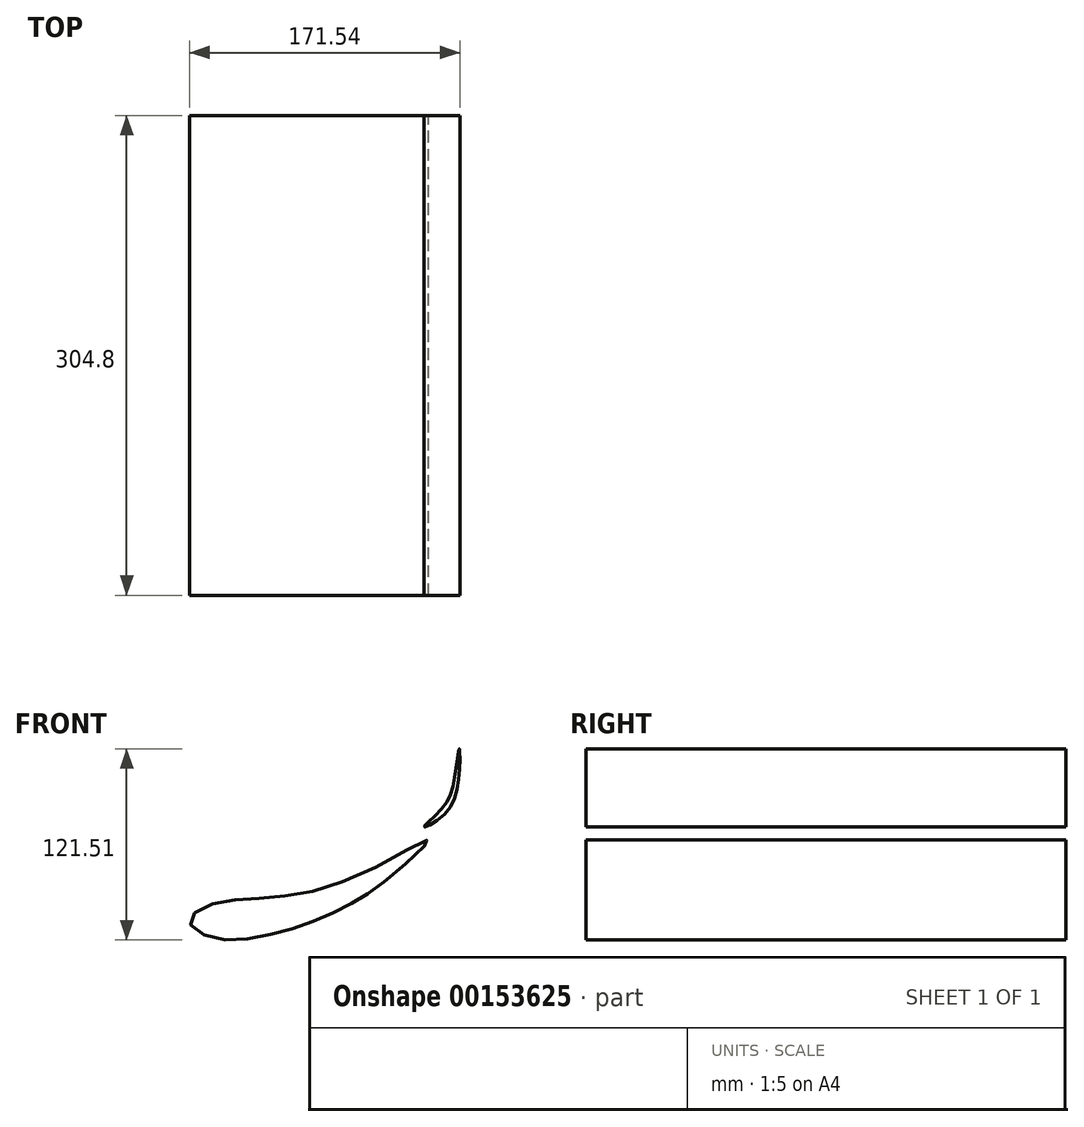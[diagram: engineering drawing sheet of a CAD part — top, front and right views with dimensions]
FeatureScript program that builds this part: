
annotation { "Feature Type Name" : "Feature", "Feature Type Description" : "" }
export const myFeature = defineFeature(function(context is Context, id is Id, definition is map)
    precondition{}
    {
        {
            var Q0;
            Q0=qCreatedBy(makeId("Front.planeOp"),FACE);
            var sketch = newSketch(context, id + "F0", { "sketchPlane" : qUnion([Q0])});
            skFitSpline(sketch, "E0", {"points": [v(0, 10.96) * mm, v(-14.47, 0) * mm, v(0, -10.55) * mm, v(33.08, -9.22) * mm, v(64.21, 0) * mm, v(90.5, 12.68) * mm, v(113.02, 28.32) * mm, v(137.26, 51.48) * mm, v(93.15, 29.42) * mm, v(37.15, 15.19) * mm, v(0, 10.96) * mm]});
            skLineSegment(sketch, "E1", {"start": v(0, 0) * mm, "end": v(138.51, 51.48) * mm, "construction": true});
            skFitSpline(sketch, "E2", {"points": [v(147.4, 68) * mm, v(156.7, 94.32) * mm, v(156.7, 109.59) * mm, v(154.04, 92.55) * mm, v(145.42, 71.32) * mm, v(134.35, 60.04) * mm, v(147.4, 68) * mm]});
            skSolve(sketch);
        }
        {
            var Q0;
            Q0=makeQuery(id+"F0.imprint","IMPRINT",FACE,{"disambiguationData":[TD([[makeQuery(id+"F0.imprint","IMPRINT",EDGE,{"derivedFrom":sQuery(id+"F0.wireOp",EDGE,"E0")}),1.0]])]});
            var Q1;
            Q1=makeQuery(id+"F0.imprint","IMPRINT",FACE,{"disambiguationData":[TD([[makeQuery(id+"F0.imprint","IMPRINT",EDGE,{"derivedFrom":sQuery(id+"F0.wireOp",EDGE,"E2")}),1.0]])]});
            extrude(context, id + "F1", {"entities" : qUnion([Q0, Q1]), "endBound" : BoundingType.SYMMETRIC, "depth" : 304.8 * mm});
        }
    });
